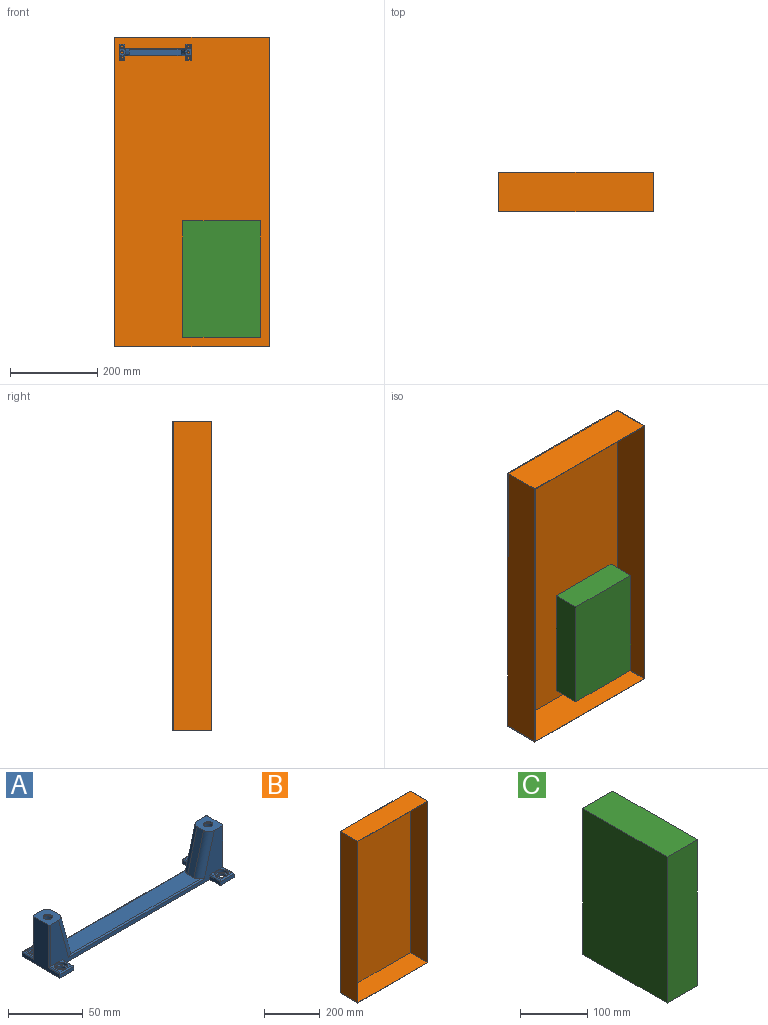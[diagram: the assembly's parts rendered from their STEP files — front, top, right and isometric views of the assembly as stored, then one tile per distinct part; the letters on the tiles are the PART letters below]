
ASSEMBLY  parts=3 mates=2
PART A: 62 faces, bbox 165x36x39.4 mm
  f0: cylinder r=4.5mm len=35.73mm, axis (0,0,-1), area 1010.1mm2, adj f14,f23
  f1: plane 11x9mm, normal (0,0,1), area 35.7mm2, adj f11,f16,f24,f26,f27
  f2: plane 11x9mm, normal (0,0,1), area 35.7mm2, adj f5,f15,f28,f29,f30
  f3: plane 9x9mm, normal (0,0,1), area 32.9mm2, adj f13,f15
  f4: plane 9x9mm, normal (0,0,1), area 32.9mm2, adj f12,f16
  f5: plane 163x38.1mm, normal (0,-1,0), area 1263.1mm2, adj f2,f6,f14,f18,f20,f28,f31,f33
  f6: plane 10x3mm, normal (-1,0,0), area 30mm2, adj f5,f7,f14,f28
  f7: plane 13x3mm, normal (0,-1,0), area 39mm2, adj f6,f8,f14,f29
  f8: plane 38.1x36mm, normal (1,0,0), area 599.4mm2, adj f7,f9,f14,f18,f25,f27,f30,f31
  f9: plane 13x3mm, normal (0,1,0), area 39mm2, adj f8,f10,f14,f26
  f10: plane 10x3mm, normal (-1,0,0), area 30mm2, adj f9,f11,f14,f24
  f11: plane 163x38.1mm, normal (0,1,0), area 1263.1mm2, adj f1,f10,f14,f18,f21,f24,f25,f32
  f12: cylinder r=3.12mm len=6.25mm, axis (0,0,-1), area 39.3mm2, adj f4,f14
  f13: cylinder r=3.12mm len=6.25mm, axis (0,0,-1), area 39.3mm2, adj f3,f14
  f14: plane 165x36mm, normal (0,0,-1), area 2910mm2, adj f0,f5,f6,f7,f8,f9,f10,f11
  f15: cylinder r=4.5mm len=9mm, axis (0,0,-1), area 56.5mm2, adj f2,f3,f29
  f16: cylinder r=4.5mm len=9mm, axis (0,0,-1), area 56.5mm2, adj f1,f4,f26
  f17: plane 123.14x14mm, normal (0,0,1), area 1676mm2, adj f19,f20,f21,f32,f33,f49,f50,f51
  f18: plane 16x13.86mm, normal (0,0,1), area 179.6mm2, adj f5,f8,f11,f19,f20,f21,f22,f25
  f19: plane 34.1x9.14mm, normal (-0.97,0,0.26), area 211.8mm2, adj f17,f18,f20,f21
  f20: cylinder r=5mm len=36.69mm, axis (-0.26,0,-0.97), area 278.6mm2, adj f5,f17,f18,f19,f33
  f21: cylinder r=5mm len=36.69mm, axis (-0.26,0,-0.97), area 278.6mm2, adj f11,f17,f18,f19,f32
  f22: cylinder r=3.12mm len=6.25mm, axis (0,0,1), area 19.6mm2, adj f18,f23
  f23: cone r=6.12mm half-angle=45deg, axis (0,0,-1), area 46.6mm2, adj f0,f22
  f24: cylinder r=1mm len=10mm, axis (0,1,0), area 15.1mm2, adj f1,f10,f11,f26
  f25: cylinder r=1mm len=35.1mm, axis (0,0,-1), area 54.1mm2, adj f8,f11,f18,f27
  f26: cylinder r=1mm len=13mm, axis (1,0,0), area 18.9mm2, adj f1,f9,f16,f24,f27
  f27: cylinder r=1mm len=11mm, axis (0,1,0), area 15.7mm2, adj f1,f8,f25,f26
  f28: cylinder r=1mm len=10mm, axis (0,1,0), area 15.1mm2, adj f2,f5,f6,f29
  f29: cylinder r=1mm len=13mm, axis (-1,0,0), area 18.9mm2, adj f2,f7,f15,f28,f30
  f30: cylinder r=1mm len=11mm, axis (0,1,0), area 15.7mm2, adj f2,f8,f29,f31
  f31: cylinder r=1mm len=35.1mm, axis (0,0,-1), area 54.1mm2, adj f5,f8,f18,f30
  f32: cylinder r=1mm len=128.82mm, axis (1,0,0), area 197.9mm2, adj f11,f17,f21,f51
  f33: cylinder r=1mm len=128.82mm, axis (-1,0,0), area 197.9mm2, adj f5,f17,f20,f50
  f34: cylinder r=4.5mm len=35.73mm, axis (0,0,-1), area 1010.1mm2, adj f14,f53
  f35: plane 11x9mm, normal (0,0,1), area 35.7mm2, adj f11,f47,f54,f56,f57
  f36: plane 11x9mm, normal (0,0,1), area 35.7mm2, adj f5,f46,f58,f59,f60
  f37: plane 9x9mm, normal (0,0,1), area 32.9mm2, adj f45,f46
  f38: plane 9x9mm, normal (0,0,1), area 32.9mm2, adj f44,f47
  f39: plane 10x3mm, normal (1,0,0), area 30mm2, adj f5,f14,f40,f58
  f40: plane 13x3mm, normal (0,-1,0), area 39mm2, adj f14,f39,f41,f59
  f41: plane 38.1x36mm, normal (-1,0,0), area 599.4mm2, adj f14,f40,f42,f48,f55,f57,f60,f61
  f42: plane 13x3mm, normal (0,1,0), area 39mm2, adj f14,f41,f43,f56
  f43: plane 10x3mm, normal (1,0,0), area 30mm2, adj f11,f14,f42,f54
  f44: cylinder r=3.12mm len=6.25mm, axis (0,0,-1), area 39.3mm2, adj f14,f38
  f45: cylinder r=3.12mm len=6.25mm, axis (0,0,-1), area 39.3mm2, adj f14,f37
  f46: cylinder r=4.5mm len=9mm, axis (0,0,-1), area 56.5mm2, adj f36,f37,f59
  f47: cylinder r=4.5mm len=9mm, axis (0,0,-1), area 56.5mm2, adj f35,f38,f56
  f48: plane 16x13.86mm, normal (0,0,1), area 179.6mm2, adj f5,f11,f41,f49,f50,f51,f52,f55
  f49: plane 34.1x9.14mm, normal (0.97,0,0.26), area 211.8mm2, adj f17,f48,f50,f51
  f50: cylinder r=5mm len=36.69mm, axis (0.26,0,-0.97), area 278.6mm2, adj f5,f17,f33,f48,f49
  f51: cylinder r=5mm len=36.69mm, axis (0.26,0,-0.97), area 278.6mm2, adj f11,f17,f32,f48,f49
  f52: cylinder r=3.12mm len=6.25mm, axis (0,0,1), area 19.6mm2, adj f48,f53
  f53: cone r=6.12mm half-angle=45deg, axis (0,0,-1), area 46.6mm2, adj f34,f52
  f54: cylinder r=1mm len=10mm, axis (0,1,0), area 15.1mm2, adj f11,f35,f43,f56
  f55: cylinder r=1mm len=35.1mm, axis (0,0,-1), area 54.1mm2, adj f11,f41,f48,f57
  f56: cylinder r=1mm len=13mm, axis (-1,0,0), area 18.9mm2, adj f35,f42,f47,f54,f57
  f57: cylinder r=1mm len=11mm, axis (0,1,0), area 15.7mm2, adj f35,f41,f55,f56
  f58: cylinder r=1mm len=10mm, axis (0,1,0), area 15.1mm2, adj f5,f36,f39,f59
  f59: cylinder r=1mm len=13mm, axis (1,0,0), area 18.9mm2, adj f36,f40,f46,f58,f60
  f60: cylinder r=1mm len=11mm, axis (0,1,0), area 15.7mm2, adj f36,f41,f59,f61
  f61: cylinder r=1mm len=35.1mm, axis (0,0,-1), area 54.1mm2, adj f5,f41,f48,f60
PART B: 11 faces, bbox 355.6x88.9x711.2 mm
  f0: plane 355.6x88.9mm, normal (0,0,1), area 31612.8mm2, adj f1,f3,f4,f5
  f1: plane 711.2x88.9mm, normal (-1,0,0), area 63225.7mm2, adj f0,f2,f4,f5
  f2: plane 355.6x88.9mm, normal (0,0,-1), area 31612.8mm2, adj f1,f3,f4,f5
  f3: plane 711.2x88.9mm, normal (1,0,0), area 63225.7mm2, adj f0,f2,f4,f5
  f4: plane 711.2x355.6mm, normal (0,-1,0), area 1725.6mm2, adj f0,f1,f2,f3,f6,f7,f8,f9
  f5: plane 711.2x355.6mm, normal (0,1,0), area 252902.7mm2, adj f0,f1,f2,f3
  f6: plane 709.58x87.63mm, normal (1,0,0), area 62180.5mm2, adj f4,f7,f9,f10
  f7: plane 353.98x87.63mm, normal (0,0,1), area 31019.3mm2, adj f4,f6,f8,f10
  f8: plane 709.58x87.63mm, normal (-1,0,0), area 62180.5mm2, adj f4,f7,f9,f10
  f9: plane 353.98x87.63mm, normal (0,0,-1), area 31019.3mm2, adj f4,f6,f8,f10
  f10: plane 709.58x353.98mm, normal (0,-1,0), area 251177.1mm2, adj f6,f7,f8,f9
PART C: 6 faces, bbox 63.5x177.8x266.7 mm
  f0: plane 177.8x63.5mm, normal (0,0,1), area 11290.3mm2, adj f1,f3,f4,f5
  f1: plane 266.7x177.8mm, normal (-1,0,0), area 47419.3mm2, adj f0,f2,f4,f5
  f2: plane 177.8x63.5mm, normal (0,0,-1), area 11290.3mm2, adj f1,f3,f4,f5
  f3: plane 266.7x177.8mm, normal (1,0,0), area 47419.3mm2, adj f0,f2,f4,f5
  f4: plane 266.7x63.5mm, normal (0,1,0), area 16935.5mm2, adj f0,f1,f2,f3
  f5: plane 266.7x63.5mm, normal (0,-1,0), area 16935.5mm2, adj f0,f1,f2,f3
PLACE A rot(axis=(1,0,0),90deg) t=(-84.41,-1.27,320.72)mm
PLACE B at identity
PLACE C rot(axis=(-0.71,0.71,0),180deg) t=(156.86,-33.02,-199.87)mm
MATE planar C.f1 <-> B.f10  axis (0,1,0) through (67.96,-1.27,-199.87)mm
MATE planar A.f14 <-> B.f10  axis (0,1,0) through (-84.41,-1.27,320.72)mm
